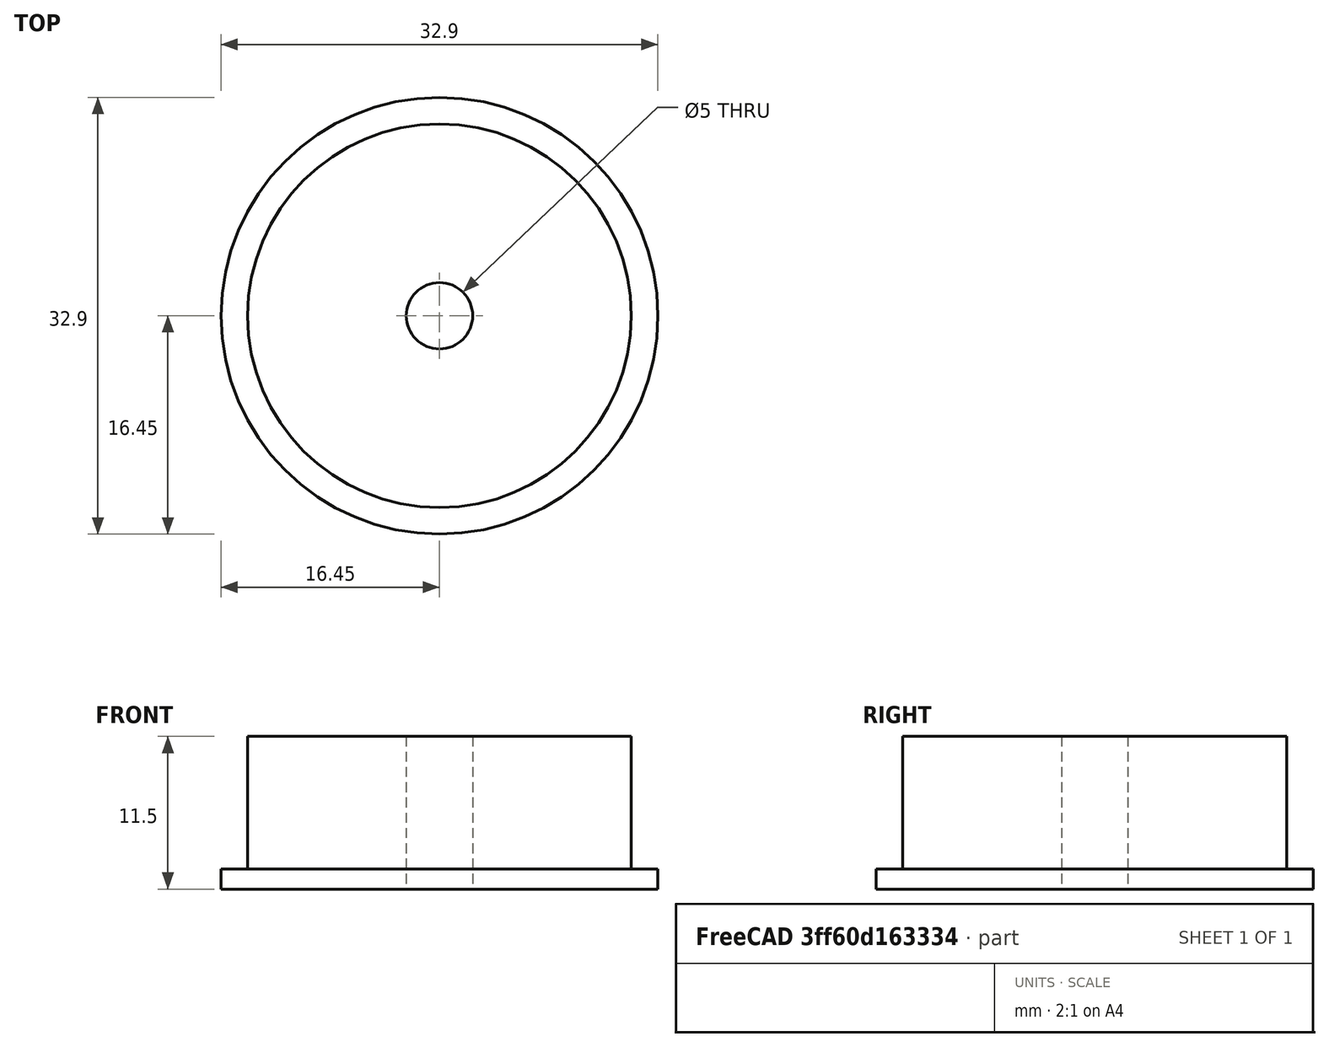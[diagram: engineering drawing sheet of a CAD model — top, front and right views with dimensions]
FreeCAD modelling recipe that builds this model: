
FCSTD DOCUMENT  (FreeCAD 0.16R4928 (Git))
Label: tapon
License: CreativeCommons Attribution-ShareAlike
LicenseURL: http://creativecommons.org/licenses/by-sa/4.0/
objects: Sketcher::SketchObject×1, PartDesign::Revolution×1
note: 3 computed .brp shape members not serialized (recipe doc carries the construction recipe); baked Part::Feature solids carry a one-line shape summary decoded from their .brp

FEATURE [Sketcher::SketchObject] Sketch
  Placement = pos=(0,0,0) rot=(-1,0,0;4.71239rad)
  sketch-geometry (6):
    g0: LineSegment StartX=2.5 StartY=11.5 StartZ=0 EndX=14.45 EndY=11.5 EndZ=0
    g1: LineSegment StartX=14.45 StartY=11.5 StartZ=0 EndX=14.45 EndY=1.5 EndZ=0
    g2: LineSegment StartX=14.45 StartY=1.5 StartZ=0 EndX=16.45 EndY=1.5 EndZ=0
    g3: LineSegment StartX=16.45 StartY=1.5 StartZ=0 EndX=16.45 EndY=0 EndZ=0
    g4: LineSegment StartX=2.5 StartY=11.5 StartZ=0 EndX=2.5 EndY=0 EndZ=0
    g5: LineSegment StartX=2.5 StartY=0 StartZ=0 EndX=16.45 EndY=0 EndZ=0
  constraints (18):
    c: Horizontal(g0)
    c: Coincident(g0,g1)
    c: Vertical(g1)
    c: Coincident(g1,g2)
    c: Coincident(g2,g3)
    c: Horizontal(g2)
    c: Vertical(g3)
    c: Coincident(g0,g4)
    c: Vertical(g4)
    c: Coincident(g4,g5)
    c: Coincident(g5,g3)
    c: Horizontal(g5)
    c: PointOnObject(g4,g-1)
    c: DistanceY(g1) = -10
    c: DistanceY(g3) = -1.5
    c: DistanceX(g1) = 14.45
    c: DistanceX(g2) = 2
    c: DistanceX(g0) = 2.5
FEATURE [PartDesign::Revolution] Revolution
  Angle = 360
  Axis = (0,0,1)
  Base = (0,0,0)
  Placement = pos=(0,0,0) rot=(-1,0,0;4.71239rad)
  ReferenceAxis = -> Sketch [V_Axis]
  Reversed = true
  Sketch = -> Sketch
